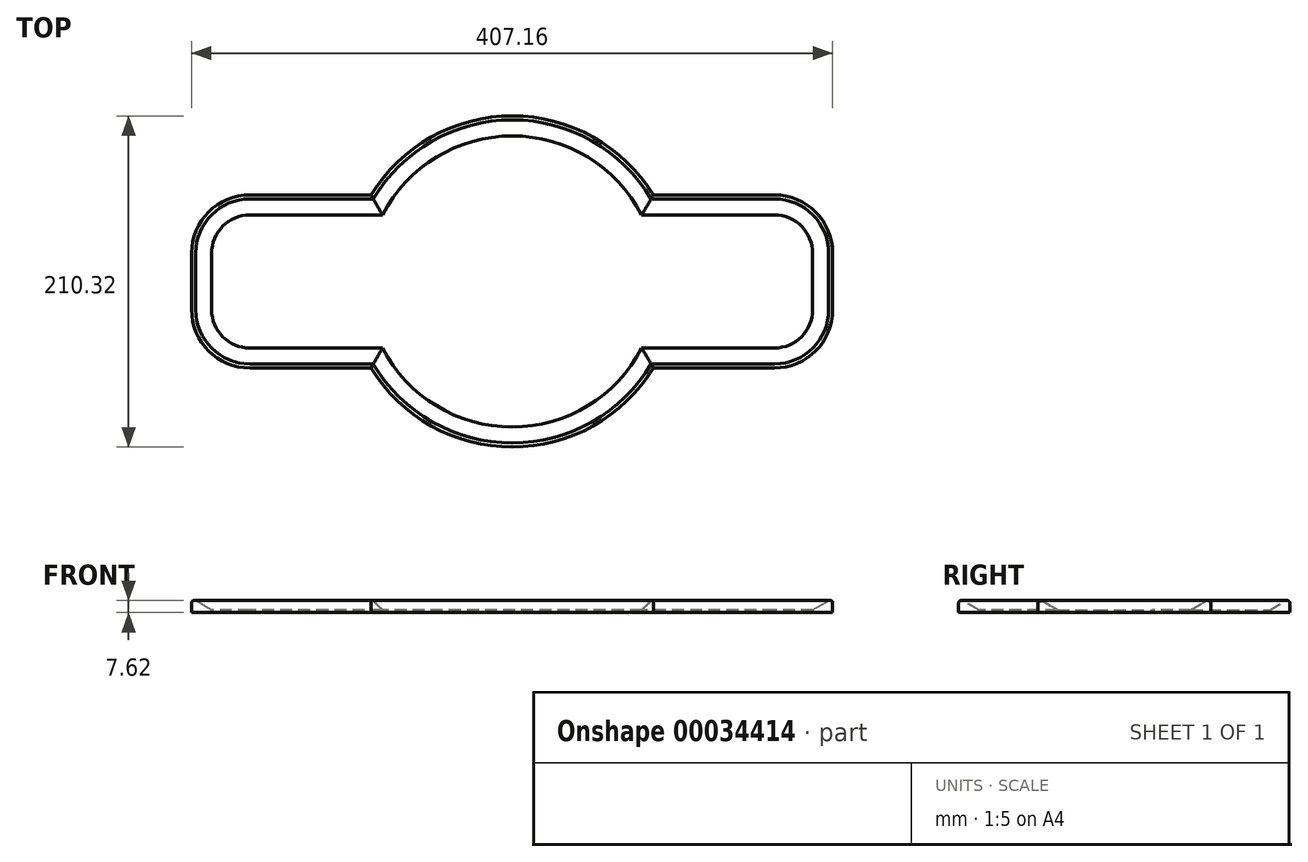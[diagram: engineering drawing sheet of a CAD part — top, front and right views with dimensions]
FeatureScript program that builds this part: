
annotation { "Feature Type Name" : "Feature", "Feature Type Description" : "" }
export const myFeature = defineFeature(function(context is Context, id is Id, definition is map)
    precondition{}
    {
        {
            var Q0;
            Q0=qCreatedBy(makeId("Front.planeOp"),FACE);
            var sketch = newSketch(context, id + "F0", { "sketchPlane" : qUnion([Q0])});
            skCircle(sketch, "E0", {"center": v(0, 0) * mm, "radius": 71.93 * mm});
            skCircle(sketch, "E1.0", {"center": v(0, 0) * mm, "radius": 81.78 * mm});
            skArc(sketch, "E2.0", {"start": v(-82.24, -42.24) * mm, "mid": v(0, -92.46) * mm, "end": v(82.24, -42.24) * mm});
            skLineSegment(sketch, "E3.rect.bottom", {"start": v(-166.6, 42.24) * mm, "end": v(-82.24, 42.24) * mm});
            skLineSegment(sketch, "E3.rect.top", {"start": v(-166.6, -42.24) * mm, "end": v(-82.24, -42.24) * mm});
            skLineSegment(sketch, "E3.rect.left", {"start": v(-190.88, 17.96) * mm, "end": v(-190.88, -17.96) * mm});
            skLineSegment(sketch, "E3.rect.right", {"start": v(190.88, 17.96) * mm, "end": v(190.88, -17.96) * mm});
            skPoint(sketch, "E4.visualSharp", {"position": v(-190.88, 42.24) * mm});
            skArc(sketch, "E4.filletArc", {"start": v(-166.6, 42.24) * mm, "mid": v(-183.77, 35.13) * mm, "end": v(-190.88, 17.96) * mm});
            skPoint(sketch, "E5.visualSharp", {"position": v(-190.88, -42.24) * mm});
            skArc(sketch, "E5.filletArc", {"start": v(-190.88, -17.96) * mm, "mid": v(-183.77, -35.13) * mm, "end": v(-166.6, -42.24) * mm});
            skPoint(sketch, "E6.visualSharp", {"position": v(190.88, -42.24) * mm});
            skArc(sketch, "E6.filletArc", {"start": v(166.6, -42.24) * mm, "mid": v(183.77, -35.13) * mm, "end": v(190.88, -17.96) * mm});
            skPoint(sketch, "E7.visualSharp", {"position": v(190.88, 42.24) * mm});
            skArc(sketch, "E7.filletArc", {"start": v(190.88, 17.96) * mm, "mid": v(183.77, 35.13) * mm, "end": v(166.6, 42.24) * mm});
            skArc(sketch, "E8.trimOffspring", {"start": v(82.24, 42.24) * mm, "mid": v(0, 92.46) * mm, "end": v(-82.24, 42.24) * mm});
            skLineSegment(sketch, "E9.trimOffspring", {"start": v(82.24, 42.24) * mm, "end": v(166.6, 42.24) * mm});
            skLineSegment(sketch, "E10.trimOffspring", {"start": v(82.24, -42.24) * mm, "end": v(166.6, -42.24) * mm});
            skLineSegment(sketch, "E11.trimOffspring", {"start": v(-70.02, -42.24) * mm, "end": v(70.02, -42.24) * mm});
            skLineSegment(sketch, "E12.trimOffspring", {"start": v(-70.02, 42.24) * mm, "end": v(70.02, 42.24) * mm});
            skArc(sketch, "E13.0", {"start": v(-203.58, -17.96) * mm, "mid": v(-192.75, -44.1) * mm, "end": v(-166.6, -54.94) * mm});
            skLineSegment(sketch, "E13.1", {"start": v(203.58, 17.96) * mm, "end": v(203.58, -17.96) * mm});
            skArc(sketch, "E13.2", {"start": v(166.6, -54.94) * mm, "mid": v(192.75, -44.1) * mm, "end": v(203.58, -17.96) * mm});
            skLineSegment(sketch, "E13.3", {"start": v(89.66, -54.94) * mm, "end": v(166.6, -54.94) * mm});
            skArc(sketch, "E13.4", {"start": v(-89.66, -54.94) * mm, "mid": v(0, -105.16) * mm, "end": v(89.66, -54.94) * mm});
            skArc(sketch, "E13.5", {"start": v(203.58, 17.96) * mm, "mid": v(192.75, 44.1) * mm, "end": v(166.6, 54.94) * mm});
            skLineSegment(sketch, "E13.6", {"start": v(-166.6, -54.94) * mm, "end": v(-89.66, -54.94) * mm});
            skLineSegment(sketch, "E13.7", {"start": v(89.66, 54.94) * mm, "end": v(166.6, 54.94) * mm});
            skArc(sketch, "E13.8", {"start": v(89.66, 54.94) * mm, "mid": v(0, 105.16) * mm, "end": v(-89.66, 54.94) * mm});
            skLineSegment(sketch, "E13.9", {"start": v(-166.6, 54.94) * mm, "end": v(-89.66, 54.94) * mm});
            skArc(sketch, "E13.10", {"start": v(-166.6, 54.94) * mm, "mid": v(-192.75, 44.1) * mm, "end": v(-203.58, 17.96) * mm});
            skLineSegment(sketch, "E13.11", {"start": v(-203.58, 17.96) * mm, "end": v(-203.58, -17.96) * mm});
            skSolve(sketch);
        }
        {
            var Q0;
            Q0=makeQuery(id+"F0.imprint","IMPRINT",FACE,{"disambiguationData":[TD([[makeQuery(id+"F0.imprint","IMPRINT",EDGE,{"derivedFrom":sQuery(id+"F0.wireOp",EDGE,"E2.0")}),-1.0]])]});
            extrude(context, id + "F1", {"entities" : qUnion([Q0]), "depth" : 7.62 * mm});
        }
        {
            var Q0;
            Q0=makeQuery(id+"F1.opExtrude","CAP_EDGE",EDGE,{"disambiguationData":[OSD([sQuery(id+"F0.wireOp",EDGE,"E3.rect.bottom")])],"isStart":false});
            var Q1;
            Q1=makeQuery(id+"F1.opExtrude","CAP_EDGE",EDGE,{"disambiguationData":[OSD([sQuery(id+"F0.wireOp",EDGE,"E8.trimOffspring")])],"isStart":false});
            var Q2;
            Q2=makeQuery(id+"F1.opExtrude","CAP_EDGE",EDGE,{"disambiguationData":[OSD([sQuery(id+"F0.wireOp",EDGE,"E9.trimOffspring")])],"isStart":false});
            var Q3;
            Q3=makeQuery(id+"F1.opExtrude","CAP_EDGE",EDGE,{"disambiguationData":[OSD([sQuery(id+"F0.wireOp",EDGE,"E7.filletArc")])],"isStart":false});
            var Q4;
            Q4=makeQuery(id+"F1.opExtrude","CAP_EDGE",EDGE,{"disambiguationData":[OSD([sQuery(id+"F0.wireOp",EDGE,"E3.rect.right")])],"isStart":false});
            var Q5;
            Q5=makeQuery(id+"F1.opExtrude","CAP_EDGE",EDGE,{"disambiguationData":[OSD([sQuery(id+"F0.wireOp",EDGE,"E6.filletArc")])],"isStart":false});
            var Q6;
            Q6=makeQuery(id+"F1.opExtrude","CAP_EDGE",EDGE,{"disambiguationData":[OSD([sQuery(id+"F0.wireOp",EDGE,"E10.trimOffspring")])],"isStart":false});
            var Q7;
            Q7=makeQuery(id+"F1.opExtrude","CAP_EDGE",EDGE,{"disambiguationData":[OSD([sQuery(id+"F0.wireOp",EDGE,"E2.0")])],"isStart":false});
            var Q8;
            Q8=makeQuery(id+"F1.opExtrude","CAP_EDGE",EDGE,{"disambiguationData":[OSD([sQuery(id+"F0.wireOp",EDGE,"E3.rect.top")])],"isStart":false});
            var Q9;
            Q9=makeQuery(id+"F1.opExtrude","CAP_EDGE",EDGE,{"disambiguationData":[OSD([sQuery(id+"F0.wireOp",EDGE,"E5.filletArc")])],"isStart":false});
            var Q10;
            Q10=makeQuery(id+"F1.opExtrude","CAP_EDGE",EDGE,{"disambiguationData":[OSD([sQuery(id+"F0.wireOp",EDGE,"E3.rect.left")])],"isStart":false});
            var Q11;
            Q11=makeQuery(id+"F1.opExtrude","CAP_EDGE",EDGE,{"disambiguationData":[OSD([sQuery(id+"F0.wireOp",EDGE,"E4.filletArc")])],"isStart":false});
            chamfer(context, id + "F2", {"entities" : qUnion([Q0, Q1, Q2, Q3, Q4, Q5, Q6, Q7, Q8, Q9, Q10, Q11]), "chamferType" : ChamferType.OFFSET_ANGLE, "width" : 10.16 * mm, "oppositeDirection" : false, "angle" : 30 * degree, "tangentPropagation" : true});
        }
        {
            var Q0;
            Q0=makeQuery(id+"F1.opExtrude","CAP_EDGE",EDGE,{"disambiguationData":[OSD([sQuery(id+"F0.wireOp",EDGE,"E13.0")])],"isStart":false});
            var Q1;
            Q1=makeQuery(id+"F1.opExtrude","CAP_EDGE",EDGE,{"disambiguationData":[OSD([sQuery(id+"F0.wireOp",EDGE,"E13.6")])],"isStart":false});
            var Q2;
            Q2=makeQuery(id+"F1.opExtrude","CAP_EDGE",EDGE,{"disambiguationData":[OSD([sQuery(id+"F0.wireOp",EDGE,"E13.4")])],"isStart":false});
            var Q3;
            Q3=makeQuery(id+"F1.opExtrude","CAP_EDGE",EDGE,{"disambiguationData":[OSD([sQuery(id+"F0.wireOp",EDGE,"E13.3")])],"isStart":false});
            var Q4;
            Q4=makeQuery(id+"F1.opExtrude","CAP_EDGE",EDGE,{"disambiguationData":[OSD([sQuery(id+"F0.wireOp",EDGE,"E13.2")])],"isStart":false});
            var Q5;
            Q5=makeQuery(id+"F1.opExtrude","CAP_EDGE",EDGE,{"disambiguationData":[OSD([sQuery(id+"F0.wireOp",EDGE,"E13.1")])],"isStart":false});
            var Q6;
            Q6=makeQuery(id+"F1.opExtrude","CAP_EDGE",EDGE,{"disambiguationData":[OSD([sQuery(id+"F0.wireOp",EDGE,"E13.5")])],"isStart":false});
            var Q7;
            Q7=makeQuery(id+"F1.opExtrude","CAP_EDGE",EDGE,{"disambiguationData":[OSD([sQuery(id+"F0.wireOp",EDGE,"E13.7")])],"isStart":false});
            var Q8;
            Q8=makeQuery(id+"F1.opExtrude","CAP_EDGE",EDGE,{"disambiguationData":[OSD([sQuery(id+"F0.wireOp",EDGE,"E13.8")])],"isStart":false});
            var Q9;
            Q9=makeQuery(id+"F1.opExtrude","CAP_EDGE",EDGE,{"disambiguationData":[OSD([sQuery(id+"F0.wireOp",EDGE,"E13.9")])],"isStart":false});
            var Q10;
            Q10=makeQuery(id+"F1.opExtrude","CAP_EDGE",EDGE,{"disambiguationData":[OSD([sQuery(id+"F0.wireOp",EDGE,"E13.10")])],"isStart":false});
            var Q11;
            Q11=makeQuery(id+"F1.opExtrude","CAP_EDGE",EDGE,{"disambiguationData":[OSD([sQuery(id+"F0.wireOp",EDGE,"E13.11")])],"isStart":false});
            fillet(context, id + "F3", {"entities" : qUnion([Q0, Q1, Q2, Q3, Q4, Q5, Q6, Q7, Q8, Q9, Q10, Q11]), "radius" : 1.52 * mm, "tangentPropagation" : true, "allowEdgeOverflow" : false});
        }
        {
            var Q0;
            Q0=makeQuery(id+"F1.opExtrude","CAP_FACE",FACE,{"disambiguationData":[OSD([sQuery(id+"F0.wireOp",EDGE,"E2.0"),sQuery(id+"F0.wireOp",EDGE,"E3.rect.bottom"),sQuery(id+"F0.wireOp",EDGE,"E3.rect.top"),sQuery(id+"F0.wireOp",EDGE,"E3.rect.left"),sQuery(id+"F0.wireOp",EDGE,"E3.rect.right"),sQuery(id+"F0.wireOp",EDGE,"E4.filletArc"),sQuery(id+"F0.wireOp",EDGE,"E5.filletArc"),sQuery(id+"F0.wireOp",EDGE,"E6.filletArc"),sQuery(id+"F0.wireOp",EDGE,"E7.filletArc"),sQuery(id+"F0.wireOp",EDGE,"E8.trimOffspring"),sQuery(id+"F0.wireOp",EDGE,"E9.trimOffspring"),sQuery(id+"F0.wireOp",EDGE,"E10.trimOffspring"),sQuery(id+"F0.wireOp",EDGE,"E13.0"),sQuery(id+"F0.wireOp",EDGE,"E13.1"),sQuery(id+"F0.wireOp",EDGE,"E13.2"),sQuery(id+"F0.wireOp",EDGE,"E13.3"),sQuery(id+"F0.wireOp",EDGE,"E13.4"),sQuery(id+"F0.wireOp",EDGE,"E13.5"),sQuery(id+"F0.wireOp",EDGE,"E13.6"),sQuery(id+"F0.wireOp",EDGE,"E13.7"),sQuery(id+"F0.wireOp",EDGE,"E13.8"),sQuery(id+"F0.wireOp",EDGE,"E13.9"),sQuery(id+"F0.wireOp",EDGE,"E13.10"),sQuery(id+"F0.wireOp",EDGE,"E13.11")])],"isStart":true});
            shell(context, id + "F4", {"entities" : qUnion([Q0]), "thickness" : 0.25 * mm});
        }
        {
            var Q0;
            {var subQ0=sQuery(id+"F0.wireOp",EDGE,"E12.trimOffspring");var subQ1=sQuery(id+"F0.wireOp",EDGE,"E0");var subQ3=makeQuery(id+"F0.imprint","INTERSECT",VERTEX,{"disambiguationData":[OD(0.0)],"derivedFrom":[subQ1,subQ0]});Q0=makeQuery(id+"F0.imprint","IMPRINT",FACE,{"disambiguationData":[TD([[makeQuery(id+"F0.imprint","IMPRINT",EDGE,{"disambiguationData":[TD([[subQ3,-1.0]])],"derivedFrom":subQ1}),1.0]])]});}
            var sketch = newSketch(context, id + "F5", { "sketchPlane" : qUnion([Q0])});
            skLineSegment(sketch, "E14", {"start": v(78.3, 0) * mm, "end": v(-86.25, 0) * mm});
            skSolve(sketch);
        }
        {
            var Q0;
            Q0=makeQuery(id+"F1.opExtrude","SWEPT_BODY",BODY,{"disambiguationData":[OSD([sQuery(id+"F0.wireOp",EDGE,"E2.0"),sQuery(id+"F0.wireOp",EDGE,"E3.rect.bottom"),sQuery(id+"F0.wireOp",EDGE,"E3.rect.top"),sQuery(id+"F0.wireOp",EDGE,"E3.rect.left"),sQuery(id+"F0.wireOp",EDGE,"E3.rect.right"),sQuery(id+"F0.wireOp",EDGE,"E4.filletArc"),sQuery(id+"F0.wireOp",EDGE,"E5.filletArc"),sQuery(id+"F0.wireOp",EDGE,"E6.filletArc"),sQuery(id+"F0.wireOp",EDGE,"E7.filletArc"),sQuery(id+"F0.wireOp",EDGE,"E8.trimOffspring"),sQuery(id+"F0.wireOp",EDGE,"E9.trimOffspring"),sQuery(id+"F0.wireOp",EDGE,"E10.trimOffspring"),sQuery(id+"F0.wireOp",EDGE,"E13.0"),sQuery(id+"F0.wireOp",EDGE,"E13.1"),sQuery(id+"F0.wireOp",EDGE,"E13.2"),sQuery(id+"F0.wireOp",EDGE,"E13.3"),sQuery(id+"F0.wireOp",EDGE,"E13.4"),sQuery(id+"F0.wireOp",EDGE,"E13.5"),sQuery(id+"F0.wireOp",EDGE,"E13.6"),sQuery(id+"F0.wireOp",EDGE,"E13.7"),sQuery(id+"F0.wireOp",EDGE,"E13.8"),sQuery(id+"F0.wireOp",EDGE,"E13.9"),sQuery(id+"F0.wireOp",EDGE,"E13.10"),sQuery(id+"F0.wireOp",EDGE,"E13.11")])]});
            var Q1;
            Q1=sQuery(id+"F5.wireOp",EDGE,"E14");
            transform(context, id + "F6", {"entities" : qUnion([Q0]), "transformType" : TransformType.ROTATION, "transformAxis" : qUnion([Q1]), "angle" : 90 * degree, "makeCopy" : false});
        }
    });
